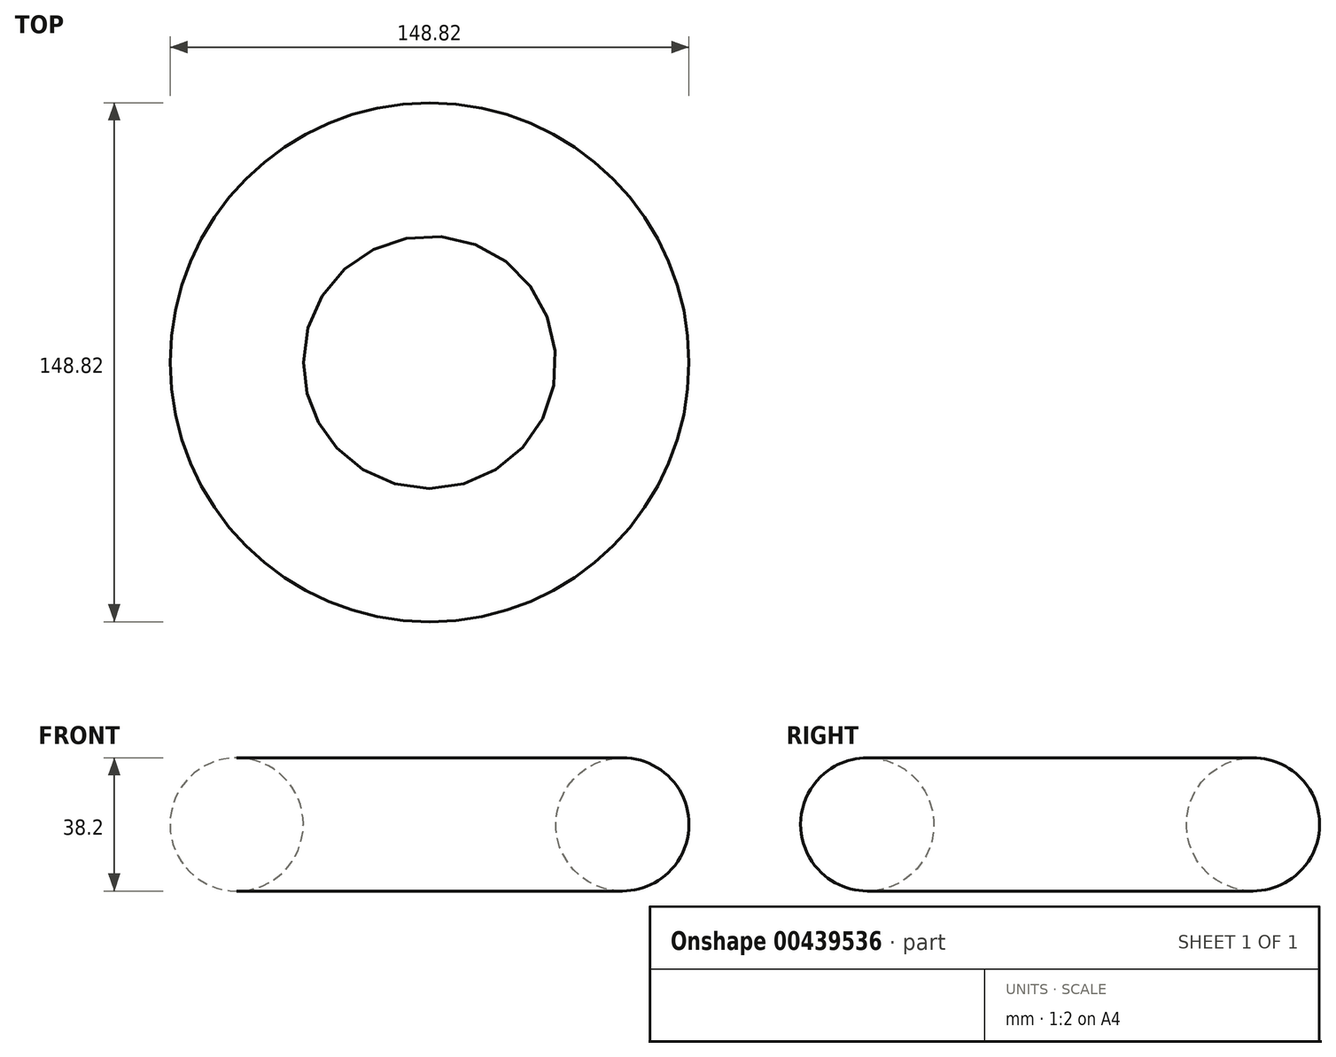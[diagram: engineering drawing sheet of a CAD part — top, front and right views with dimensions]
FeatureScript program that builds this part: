
annotation { "Feature Type Name" : "Feature", "Feature Type Description" : "" }
export const myFeature = defineFeature(function(context is Context, id is Id, definition is map)
    precondition{}
    {
        {
            var Q0;
            Q0=qCreatedBy(makeId("Front.planeOp"),FACE);
            var sketch = newSketch(context, id + "F0", { "sketchPlane" : qUnion([Q0])});
            skCircle(sketch, "E0", {"center": v(55.3, 0) * mm, "radius": 19.1 * mm});
            skSolve(sketch);
        }
        {
            var Q0;
            Q0=qCreatedBy(makeId("Front.planeOp"),FACE);
            var sketch = newSketch(context, id + "F1", { "sketchPlane" : qUnion([Q0])});
            skLineSegment(sketch, "E1", {"start": v(0, 0) * mm, "end": v(0, 42.03) * mm, "construction": true});
            skSolve(sketch);
        }
        {
            var Q0;
            Q0=makeQuery(id+"F0.imprint","IMPRINT",FACE,{"disambiguationData":[TD([[makeQuery(id+"F0.imprint","IMPRINT",EDGE,{"derivedFrom":sQuery(id+"F0.wireOp",EDGE,"E0")}),1.0]])]});
            var Q1;
            Q1=sQuery(id+"F1.wireOp",EDGE,"E1");
            revolve(context, id + "F2", {"entities" : qUnion([Q0]), "axis" : qUnion([Q1]), "revolveType" : RevolveType.FULL});
        }
    });
